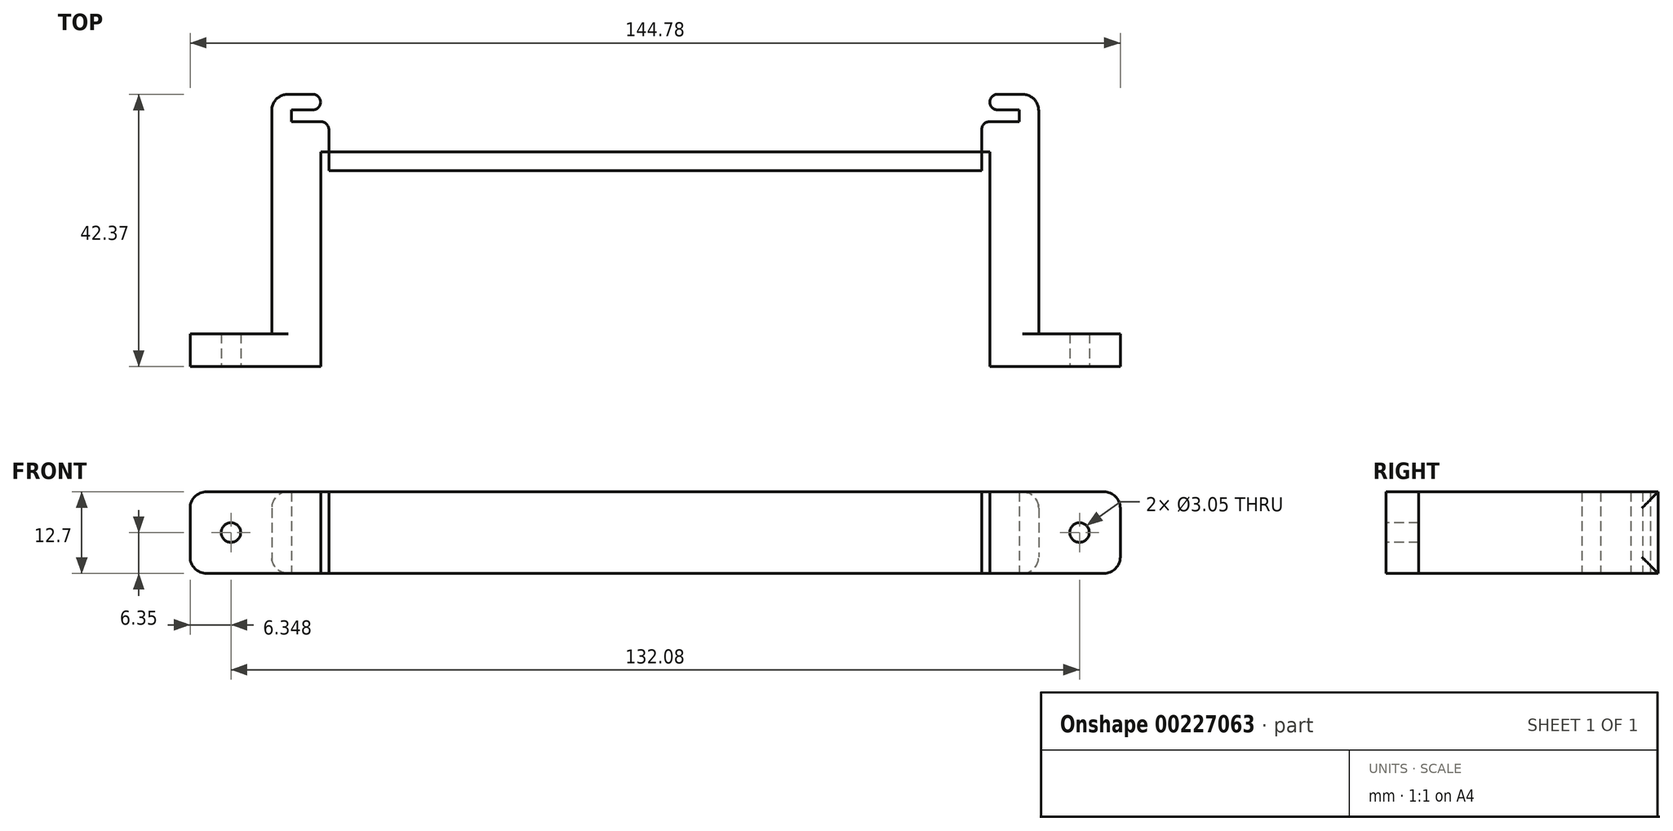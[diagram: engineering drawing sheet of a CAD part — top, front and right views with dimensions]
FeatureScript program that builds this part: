
annotation { "Feature Type Name" : "Feature", "Feature Type Description" : "" }
export const myFeature = defineFeature(function(context is Context, id is Id, definition is map)
    precondition{}
    {
        {
            var Q0;
            Q0=qCreatedBy(makeId("Top.planeOp"),FACE);
            var sketch = newSketch(context, id + "F0", { "sketchPlane" : qUnion([Q0])});
            skLineSegment(sketch, "E0.bottom", {"start": v(-54.84, 22.79) * mm, "end": v(64.54, 22.79) * mm});
            skLineSegment(sketch, "E0.top", {"start": v(-54.84, -19.58) * mm, "end": v(64.54, -19.58) * mm});
            skLineSegment(sketch, "E0.left", {"start": v(-54.84, 22.79) * mm, "end": v(-54.84, -19.58) * mm});
            skLineSegment(sketch, "E0.right", {"start": v(64.54, 22.79) * mm, "end": v(64.54, -19.58) * mm});
            skLineSegment(sketch, "E1.bottom", {"start": v(77.24, -19.58) * mm, "end": v(-67.54, -19.58) * mm});
            skLineSegment(sketch, "E1.top", {"start": v(77.24, -14.5) * mm, "end": v(-67.54, -14.5) * mm});
            skLineSegment(sketch, "E1.left", {"start": v(77.24, -19.58) * mm, "end": v(77.24, -14.5) * mm});
            skLineSegment(sketch, "E1.right", {"start": v(-67.54, -19.58) * mm, "end": v(-67.54, -14.5) * mm});
            skLineSegment(sketch, "E2.bottom", {"start": v(-47.22, 22.79) * mm, "end": v(56.92, 22.79) * mm});
            skLineSegment(sketch, "E2.top", {"start": v(-47.22, -14.5) * mm, "end": v(56.92, -14.5) * mm});
            skLineSegment(sketch, "E2.left", {"start": v(-47.22, 22.79) * mm, "end": v(-47.22, -14.5) * mm});
            skLineSegment(sketch, "E2.right", {"start": v(56.92, 22.79) * mm, "end": v(56.92, -14.5) * mm});
            skLineSegment(sketch, "E3", {"start": v(-51.8, 22.79) * mm, "end": v(-51.8, -14.5) * mm, "construction": true});
            skLineSegment(sketch, "E4", {"start": v(61.5, 22.79) * mm, "end": v(61.5, -14.5) * mm, "construction": true});
            skLineSegment(sketch, "E5", {"start": v(-54.84, 20.34) * mm, "end": v(64.54, 20.34) * mm, "construction": true});
            skLineSegment(sketch, "E6", {"start": v(-54.84, 18.52) * mm, "end": v(64.54, 18.52) * mm, "construction": true});
            skLineSegment(sketch, "E7.bottom", {"start": v(-47.22, 18.52) * mm, "end": v(-51.8, 18.52) * mm});
            skLineSegment(sketch, "E7.top", {"start": v(-47.22, 20.34) * mm, "end": v(-51.8, 20.34) * mm});
            skLineSegment(sketch, "E7.left", {"start": v(-47.22, 18.52) * mm, "end": v(-47.22, 20.34) * mm});
            skLineSegment(sketch, "E7.right", {"start": v(-51.8, 18.52) * mm, "end": v(-51.8, 20.34) * mm});
            skLineSegment(sketch, "E8.bottom", {"start": v(56.92, 20.34) * mm, "end": v(61.5, 20.34) * mm});
            skLineSegment(sketch, "E8.top", {"start": v(56.92, 18.52) * mm, "end": v(61.5, 18.52) * mm});
            skLineSegment(sketch, "E8.left", {"start": v(56.92, 20.34) * mm, "end": v(56.92, 18.52) * mm});
            skLineSegment(sketch, "E8.right", {"start": v(61.5, 20.34) * mm, "end": v(61.5, 18.52) * mm});
            skLineSegment(sketch, "E9.bottom", {"start": v(-47.22, 18.52) * mm, "end": v(-45.95, 18.52) * mm});
            skLineSegment(sketch, "E9.top", {"start": v(-47.22, 10.9) * mm, "end": v(-45.95, 10.9) * mm});
            skLineSegment(sketch, "E9.left", {"start": v(-47.22, 18.52) * mm, "end": v(-47.22, 10.9) * mm});
            skLineSegment(sketch, "E9.right", {"start": v(-45.95, 18.52) * mm, "end": v(-45.95, 10.9) * mm});
            skLineSegment(sketch, "E10.bottom", {"start": v(56.92, 18.52) * mm, "end": v(55.65, 18.52) * mm});
            skLineSegment(sketch, "E10.top", {"start": v(56.92, 10.9) * mm, "end": v(55.65, 10.9) * mm});
            skLineSegment(sketch, "E10.left", {"start": v(56.92, 18.52) * mm, "end": v(56.92, 10.9) * mm});
            skLineSegment(sketch, "E10.right", {"start": v(55.65, 18.52) * mm, "end": v(55.65, 10.9) * mm});
            skLineSegment(sketch, "E11.bottom", {"start": v(-47.22, 10.9) * mm, "end": v(56.92, 10.9) * mm});
            skLineSegment(sketch, "E11.top", {"start": v(-47.22, 13.83) * mm, "end": v(56.92, 13.83) * mm});
            skLineSegment(sketch, "E11.left", {"start": v(-47.22, 13.83) * mm, "end": v(-47.22, 10.9) * mm});
            skLineSegment(sketch, "E11.right", {"start": v(56.92, 13.83) * mm, "end": v(56.92, 10.9) * mm});
            skLineSegment(sketch, "E12", {"start": v(-47.22, -14.5) * mm, "end": v(-47.22, -19.58) * mm});
            skLineSegment(sketch, "E13", {"start": v(56.92, -14.5) * mm, "end": v(56.92, -19.58) * mm});
            skSolve(sketch);
        }
        {
            var Q0;
            {var subQ5=sQuery(id+"F0.wireOp",EDGE,"E1.right");Q0=makeQuery(id+"F0.imprint","IMPRINT",FACE,{"disambiguationData":[TD([[makeQuery(id+"F0.imprint","IMPRINT",EDGE,{"derivedFrom":subQ5}),-1.0]])]});}
            var Q1;
            {var subQ5=sQuery(id+"F0.wireOp",EDGE,"E1.left");Q1=makeQuery(id+"F0.imprint","IMPRINT",FACE,{"disambiguationData":[TD([[makeQuery(id+"F0.imprint","IMPRINT",EDGE,{"derivedFrom":subQ5}),1.0]])]});}
            var Q2;
            Q2=makeQuery(id+"F0.imprint","IMPRINT",FACE,{"disambiguationData":[TD([[makeQuery(id+"F0.imprint","IMPRINT",EDGE,{"derivedFrom":sQuery(id+"F0.wireOp",EDGE,"E7.bottom")}),1.0]])]});
            var Q3;
            {var subQ7=sQuery(id+"F0.wireOp",EDGE,"E8.bottom");Q3=makeQuery(id+"F0.imprint","IMPRINT",FACE,{"disambiguationData":[TD([[makeQuery(id+"F0.imprint","IMPRINT",EDGE,{"derivedFrom":subQ7}),1.0]])]});}
            var Q4;
            Q4=makeQuery(id+"F0.imprint","IMPRINT",FACE,{"disambiguationData":[TD([[makeQuery(id+"F0.imprint","IMPRINT",EDGE,{"derivedFrom":sQuery(id+"F0.wireOp",EDGE,"E9.bottom")}),-1.0]])]});
            var Q5;
            Q5=makeQuery(id+"F0.imprint","IMPRINT",FACE,{"disambiguationData":[TD([[makeQuery(id+"F0.imprint","IMPRINT",EDGE,{"derivedFrom":sQuery(id+"F0.wireOp",EDGE,"E10.bottom")}),1.0]])]});
            var Q6;
            Q6=makeQuery(id+"F0.imprint","IMPRINT",FACE,{"disambiguationData":[TD([[makeQuery(id+"F0.imprint","IMPRINT",EDGE,{"derivedFrom":sQuery(id+"F0.wireOp",EDGE,"E11.top")}),1.0]])]});
            var Q7;
            {var subQ5=sQuery(id+"F0.wireOp",EDGE,"E12");Q7=makeQuery(id+"F0.imprint","IMPRINT",FACE,{"disambiguationData":[TD([[makeQuery(id+"F0.imprint","IMPRINT",EDGE,{"derivedFrom":subQ5}),-1.0]])]});}
            var Q8;
            {var subQ5=sQuery(id+"F0.wireOp",EDGE,"E13");Q8=makeQuery(id+"F0.imprint","IMPRINT",FACE,{"disambiguationData":[TD([[makeQuery(id+"F0.imprint","IMPRINT",EDGE,{"derivedFrom":subQ5}),1.0]])]});}
            var Q9;
            {var subQ5=sQuery(id+"F0.wireOp",EDGE,"E11.left");Q9=makeQuery(id+"F0.imprint","IMPRINT",FACE,{"disambiguationData":[TD([[makeQuery(id+"F0.imprint","IMPRINT",EDGE,{"derivedFrom":subQ5}),1.0]])]});}
            var Q10;
            {var subQ0=sQuery(id+"F0.wireOp",EDGE,"E11.bottom");var subQ1=sQuery(id+"F0.wireOp",EDGE,"E9.right");var subQ2=makeQuery(id+"F0.imprint","INTERSECT",VERTEX,{"derivedFrom":[subQ1,subQ0]});Q10=makeQuery(id+"F0.imprint","IMPRINT",FACE,{"disambiguationData":[TD([[makeQuery(id+"F0.imprint","IMPRINT",EDGE,{"disambiguationData":[TD([[subQ2,1.0]])],"derivedFrom":subQ1}),1.0]])]});}
            var Q11;
            {var subQ5=sQuery(id+"F0.wireOp",EDGE,"E11.right");Q11=makeQuery(id+"F0.imprint","IMPRINT",FACE,{"disambiguationData":[TD([[makeQuery(id+"F0.imprint","IMPRINT",EDGE,{"derivedFrom":subQ5}),-1.0]])]});}
            extrude(context, id + "F1", {"entities" : qUnion([Q0, Q1, Q2, Q3, Q4, Q5, Q6, Q7, Q8, Q9, Q10, Q11]), "depth" : 12.7 * mm});
        }
        {
            var Q0;
            Q0=makeQuery(id+"F1.opExtrude","SWEPT_EDGE",EDGE,{"disambiguationData":[OSD([sQuery(id+"F0.wireOp",EDGE,"E0.bottom"),sQuery(id+"F0.wireOp",EDGE,"E2.bottom"),sQuery(id+"F0.wireOp",EDGE,"E2.left")])]});
            var Q1;
            Q1=makeQuery(id+"F1.opExtrude","SWEPT_EDGE",EDGE,{"disambiguationData":[OSD([sQuery(id+"F0.wireOp",EDGE,"E9.bottom"),sQuery(id+"F0.wireOp",EDGE,"E9.right")])]});
            var Q2;
            Q2=makeQuery(id+"F1.opExtrude","SWEPT_EDGE",EDGE,{"disambiguationData":[OSD([sQuery(id+"F0.wireOp",EDGE,"E2.left"),sQuery(id+"F0.wireOp",EDGE,"E7.top"),sQuery(id+"F0.wireOp",EDGE,"E7.left")])]});
            var Q3;
            Q3=makeQuery(id+"F1.opExtrude","SWEPT_EDGE",EDGE,{"disambiguationData":[OSD([sQuery(id+"F0.wireOp",EDGE,"E10.bottom"),sQuery(id+"F0.wireOp",EDGE,"E10.right")])]});
            var Q4;
            Q4=makeQuery(id+"F1.opExtrude","SWEPT_EDGE",EDGE,{"disambiguationData":[OSD([sQuery(id+"F0.wireOp",EDGE,"E2.right"),sQuery(id+"F0.wireOp",EDGE,"E8.bottom"),sQuery(id+"F0.wireOp",EDGE,"E8.left")])]});
            var Q5;
            Q5=makeQuery(id+"F1.opExtrude","SWEPT_EDGE",EDGE,{"disambiguationData":[OSD([sQuery(id+"F0.wireOp",EDGE,"E0.bottom"),sQuery(id+"F0.wireOp",EDGE,"E2.bottom"),sQuery(id+"F0.wireOp",EDGE,"E2.right")])]});
            fillet(context, id + "F2", {"entities" : qUnion([Q0, Q1, Q2, Q3, Q4, Q5]), "radius" : 1.27 * mm, "tangentPropagation" : true, "allowEdgeOverflow" : false});
        }
        {
            var Q0;
            Q0=makeQuery(id+"F1.opExtrude","SWEPT_FACE",FACE,{"disambiguationData":[OSD([sQuery(id+"F0.wireOp",EDGE,"E1.bottom")])]});
            var sketch = newSketch(context, id + "F3", { "sketchPlane" : qUnion([Q0])});
            skLineSegment(sketch, "E14", {"start": v(-67.54, 6.35) * mm, "end": v(77.24, 6.35) * mm, "construction": true});
            skLineSegment(sketch, "E15", {"start": v(-61.2, 12.7) * mm, "end": v(-61.2, 0) * mm, "construction": true});
            skLineSegment(sketch, "E16", {"start": v(70.89, 12.7) * mm, "end": v(70.89, 0) * mm, "construction": true});
            skCircle(sketch, "E17", {"center": v(-61.2, 6.35) * mm, "radius": 1.52 * mm});
            skCircle(sketch, "E18", {"center": v(70.89, 6.35) * mm, "radius": 1.52 * mm});
            skSolve(sketch);
        }
        {
            var Q0;
            Q0=makeQuery(id+"F3.imprint","IMPRINT",FACE,{"disambiguationData":[TD([[makeQuery(id+"F3.imprint","IMPRINT",EDGE,{"derivedFrom":sQuery(id+"F3.wireOp",EDGE,"E17")}),1.0]])]});
            var Q1;
            Q1=makeQuery(id+"F3.imprint","IMPRINT",FACE,{"disambiguationData":[TD([[makeQuery(id+"F3.imprint","IMPRINT",EDGE,{"derivedFrom":sQuery(id+"F3.wireOp",EDGE,"E18")}),1.0]])]});
            extrude(context, id + "F4", {"entities" : qUnion([Q0, Q1]), "operationType" : NewBodyOperationType.REMOVE, "oppositeDirection" : true, "depth" : 25.4 * mm});
        }
        {
            var Q0;
            Q0=makeQuery(id+"F1.opExtrude","CAP_EDGE",EDGE,{"disambiguationData":[OSD([sQuery(id+"F0.wireOp",EDGE,"E1.left")])],"isStart":false});
            var Q1;
            Q1=makeQuery(id+"F1.opExtrude","CAP_EDGE",EDGE,{"disambiguationData":[OSD([sQuery(id+"F0.wireOp",EDGE,"E1.left")])],"isStart":true});
            var Q2;
            Q2=makeQuery(id+"F1.opExtrude","SWEPT_EDGE",EDGE,{"disambiguationData":[OSD([sQuery(id+"F0.wireOp",EDGE,"E0.bottom"),sQuery(id+"F0.wireOp",EDGE,"E0.right")])]});
            var Q3;
            Q3=makeQuery(id+"F1.opExtrude","SWEPT_EDGE",EDGE,{"disambiguationData":[OSD([sQuery(id+"F0.wireOp",EDGE,"E0.bottom"),sQuery(id+"F0.wireOp",EDGE,"E0.left")])]});
            var Q4;
            Q4=makeQuery(id+"F1.opExtrude","CAP_EDGE",EDGE,{"disambiguationData":[OSD([sQuery(id+"F0.wireOp",EDGE,"E1.right")])],"isStart":true});
            var Q5;
            Q5=makeQuery(id+"F1.opExtrude","CAP_EDGE",EDGE,{"disambiguationData":[OSD([sQuery(id+"F0.wireOp",EDGE,"E1.right")])],"isStart":false});
            var Q6;
            Q6=makeQuery(id+"F1.opExtrude","CAP_EDGE",EDGE,{"disambiguationData":[OSD([sQuery(id+"F0.wireOp",EDGE,"E0.left")])],"isStart":true});
            var Q7;
            Q7=makeQuery(id+"F1.opExtrude","CAP_EDGE",EDGE,{"disambiguationData":[OSD([sQuery(id+"F0.wireOp",EDGE,"E0.left")])],"isStart":false});
            var Q8;
            Q8=makeQuery(id+"F1.opExtrude","CAP_EDGE",EDGE,{"disambiguationData":[OSD([sQuery(id+"F0.wireOp",EDGE,"E0.right")])],"isStart":true});
            var Q9;
            Q9=makeQuery(id+"F1.opExtrude","CAP_EDGE",EDGE,{"disambiguationData":[OSD([sQuery(id+"F0.wireOp",EDGE,"E0.right")])],"isStart":false});
            fillet(context, id + "F5", {"entities" : qUnion([Q0, Q1, Q2, Q3, Q4, Q5, Q6, Q7, Q8, Q9]), "radius" : 2.54 * mm, "tangentPropagation" : true, "allowEdgeOverflow" : false});
        }
    });
